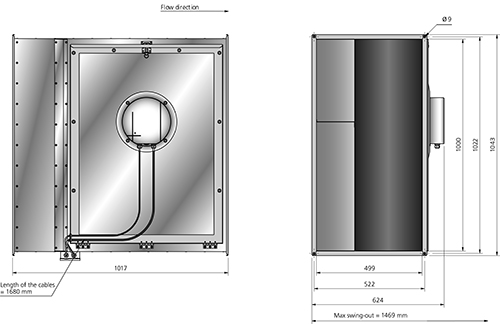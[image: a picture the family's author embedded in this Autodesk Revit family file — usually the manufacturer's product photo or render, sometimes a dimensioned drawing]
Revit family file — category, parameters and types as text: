
# Revit family: RKB 1000x500 F3 EC_7480109
name_source: partatom
category: Mechanical Equipment
revit_build: Autodesk Revit MEP 2014 (Build: 20130308_1515(x64)
units: mm (PartAtom-declared; Revit-internal decimal feet)

## types (1)
- RKB 1000X500 F3 EC
    Capacitor = - μF
    Connector Height = 500 mm  [stored 1.64042 ft]
    Connector Width = 1000 mm  [stored 3.28084 ft]
    Current = 5 A
    Depth = 1043 mm  [stored 3.42192 ft]
    Description = UNINSULATED DUCT FANS WITH RECTANGULAR CONNECTIONS
    Frequency = 50 Hz
    Height = 624 mm  [stored 2.04724 ft]
    Main Material = Steel, Galvanized
    Max. temperature of transported air = 60 °C
    Max. temperature of transported air when speed controlled = 60 °C
    Phase = 3
    Power = 3450 W
    Sound pressure level at 3 m = 73 dB(A)
    Speed = 1630 rpm
    Voltage = 400 V
    Voltage range = 380-480 V
    Weight = 83.30 kg
    Width = 1017 mm  [stored 3.33661 ft]
    Wiring diagram = 4040147

note: [stored X ft] marks values corroborated as IEEE doubles in the binary element streams (Revit-internal decimal feet)

## geometry (parser evidence)
native form markers: Sweep x4
no freeform markers — native parametric forms only
